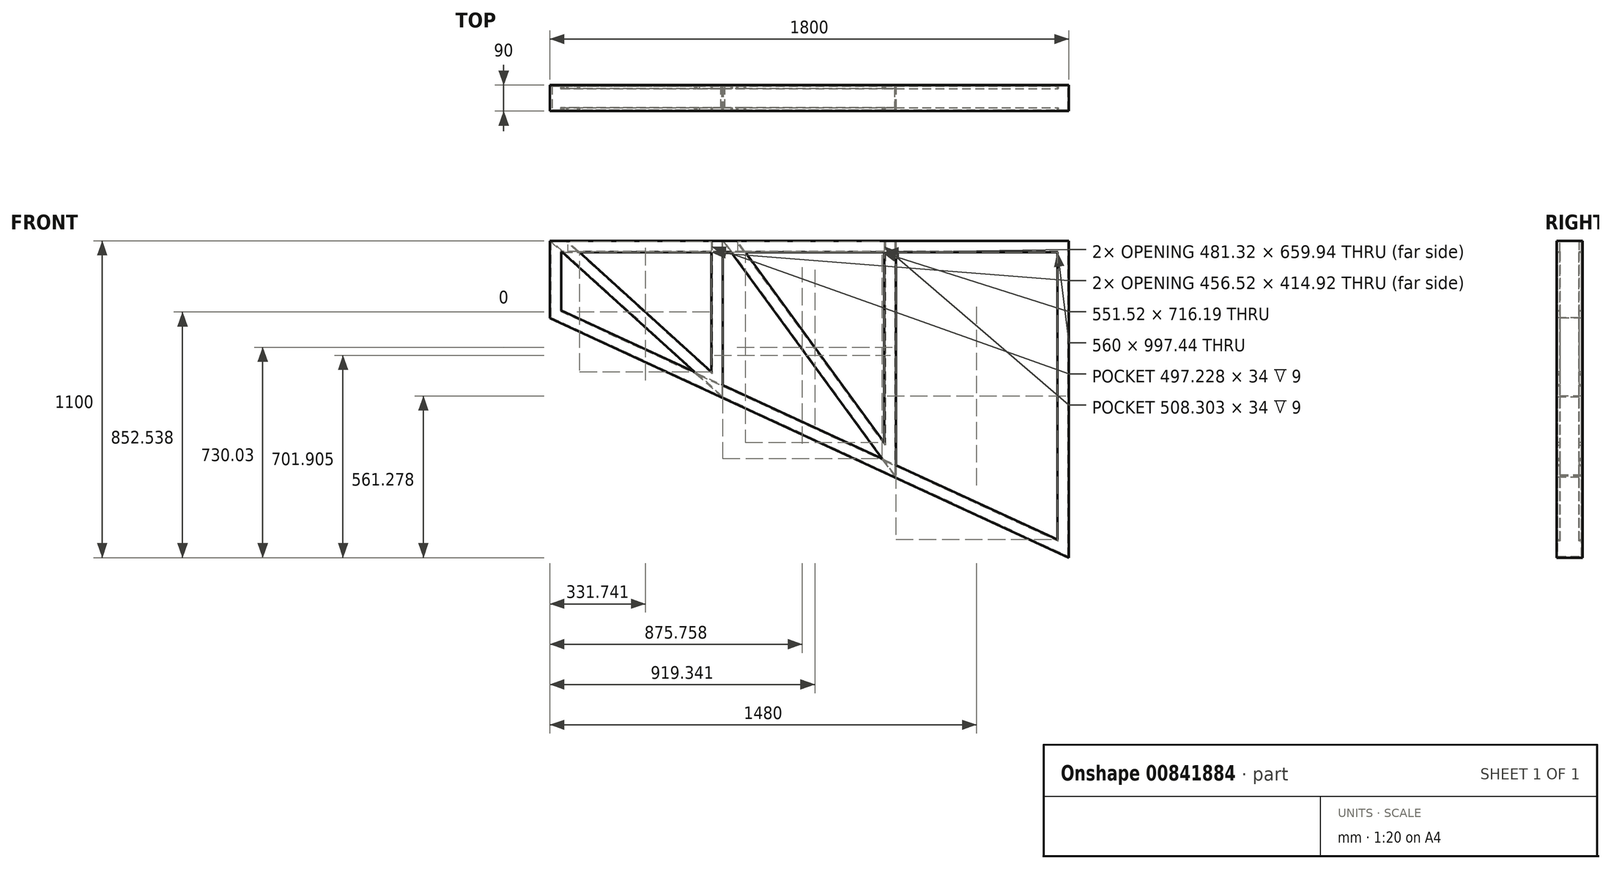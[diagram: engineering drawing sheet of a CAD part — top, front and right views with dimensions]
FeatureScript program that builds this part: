
annotation { "Feature Type Name" : "Feature", "Feature Type Description" : "" }
export const myFeature = defineFeature(function(context is Context, id is Id, definition is map)
    precondition{}
    {
        {
            var Q0;
            Q0=qCreatedBy(makeId("Front.planeOp"),FACE);
            var sketch = newSketch(context, id + "F0", { "sketchPlane" : qUnion([Q0])});
            skLineSegment(sketch, "E0", {"start": v(0, 0) * mm, "end": v(0, 1100) * mm});
            skLineSegment(sketch, "E1", {"start": v(0, 1100) * mm, "end": v(-1800, 1100) * mm});
            skLineSegment(sketch, "E2", {"start": v(-1800, 1100) * mm, "end": v(-1800, 832) * mm});
            skLineSegment(sketch, "E3", {"start": v(-1800, 832) * mm, "end": v(0, 0) * mm});
            skSolve(sketch);
        }
        {
            var Q0;
            Q0=qCreatedBy(makeId("Top.planeOp"),FACE);
            var sketch = newSketch(context, id + "F1", { "sketchPlane" : qUnion([Q0])});
            skLineSegment(sketch, "E4", {"start": v(0, 0) * mm, "end": v(0, -45) * mm});
            skLineSegment(sketch, "E5", {"start": v(0, -45) * mm, "end": v(-40, -45) * mm});
            skLineSegment(sketch, "E6", {"start": v(-40, -45) * mm, "end": v(-40, -33) * mm});
            skLineSegment(sketch, "E7.MirrorCS", {"start": v(-40, 45) * mm, "end": v(-40, 33) * mm});
            skLineSegment(sketch, "E8.MirrorCS", {"start": v(0, 45) * mm, "end": v(-40, 45) * mm});
            skLineSegment(sketch, "E9.MirrorCS", {"start": v(0, 0) * mm, "end": v(0, 45) * mm});
            skLineSegment(sketch, "E10.0", {"start": v(-37, -42) * mm, "end": v(-37, -33) * mm});
            skLineSegment(sketch, "E10.1", {"start": v(-3, -42) * mm, "end": v(-37, -42) * mm});
            skLineSegment(sketch, "E10.2", {"start": v(-37, 42) * mm, "end": v(-37, 33) * mm});
            skLineSegment(sketch, "E10.3", {"start": v(-3, 42) * mm, "end": v(-37, 42) * mm});
            skLineSegment(sketch, "E10.4", {"start": v(-3, 0) * mm, "end": v(-3, 42) * mm});
            skLineSegment(sketch, "E10.5", {"start": v(-3, 0) * mm, "end": v(-3, -42) * mm});
            skLineSegment(sketch, "E11", {"start": v(-40, -33) * mm, "end": v(-37, -33) * mm});
            skLineSegment(sketch, "E12", {"start": v(-40, 33) * mm, "end": v(-37, 33) * mm});
            skSolve(sketch);
        }
        {
            var Q0;
            Q0 = qSketchRegion(id + "F1", true);
            var Q1;
            Q1 = qConstructionFilter(qBodyType(qCreatedBy(id + "F0" ,EDGE), BodyType.WIRE), ConstructionObject.NO);
            sweep(context, id + "F2", {"profiles" : qUnion([Q0]), "path" : qUnion([Q1])});
        }
        {
            var Q0;
            Q0=qCreatedBy(makeId("Front.planeOp"),FACE);
            var sketch = newSketch(context, id + "F3", { "sketchPlane" : qUnion([Q0])});
            skLineSegment(sketch, "E13", {"start": v(-600, 1100) * mm, "end": v(-600, 277.33) * mm});
            skLineSegment(sketch, "E14", {"start": v(-600, 277.33) * mm, "end": v(-1200, 1100) * mm});
            skLineSegment(sketch, "E15", {"start": v(-1200, 1100) * mm, "end": v(-1200, 554.67) * mm});
            skLineSegment(sketch, "E16", {"start": v(-1200, 554.67) * mm, "end": v(-1800, 1100) * mm});
            skSolve(sketch);
        }
        {
            var Q0;
            Q0=makeQuery(id+"F2.opSweep","SWEPT_FACE",FACE,{"disambiguationData":[OSD([sQuery(id+"F0.wireOp",EDGE,"E1"),sQuery(id+"F1.wireOp",EDGE,"E4"),sQuery(id+"F1.wireOp",EDGE,"E9.MirrorCS")])]});
            var sketch = newSketch(context, id + "F4", { "sketchPlane" : qUnion([Q0])});
            skLineSegment(sketch, "E17", {"start": v(-600, 0) * mm, "end": v(-600, 45) * mm});
            skLineSegment(sketch, "E18", {"start": v(-600, 45) * mm, "end": v(-640, 45) * mm});
            skLineSegment(sketch, "E19", {"start": v(-640, 45) * mm, "end": v(-640, 33) * mm});
            skLineSegment(sketch, "E20.MirrorCS", {"start": v(-640, -45) * mm, "end": v(-640, -33) * mm});
            skLineSegment(sketch, "E21.MirrorCS", {"start": v(-600, -45) * mm, "end": v(-640, -45) * mm});
            skLineSegment(sketch, "E22.MirrorCS", {"start": v(-600, 0) * mm, "end": v(-600, -45) * mm});
            skLineSegment(sketch, "E23.0", {"start": v(-637, 42) * mm, "end": v(-637, 33) * mm});
            skLineSegment(sketch, "E23.1", {"start": v(-603, 42) * mm, "end": v(-637, 42) * mm});
            skLineSegment(sketch, "E23.2", {"start": v(-637, -42) * mm, "end": v(-637, -33) * mm});
            skLineSegment(sketch, "E23.3", {"start": v(-603, -42) * mm, "end": v(-637, -42) * mm});
            skLineSegment(sketch, "E23.4", {"start": v(-603, 0) * mm, "end": v(-603, -42) * mm});
            skLineSegment(sketch, "E23.5", {"start": v(-603, 0) * mm, "end": v(-603, 42) * mm});
            skLineSegment(sketch, "E24", {"start": v(-640, 33) * mm, "end": v(-637, 33) * mm});
            skLineSegment(sketch, "E25", {"start": v(-637, -33) * mm, "end": v(-640, -33) * mm});
            skSolve(sketch);
        }
        {
            var Q0;
            Q0 = qSketchRegion(id + "F4", true);
            var Q1;
            Q1 = qConstructionFilter(qBodyType(qCreatedBy(id + "F3" ,EDGE), BodyType.WIRE), ConstructionObject.NO);
            sweep(context, id + "F5", {"operationType" : NewBodyOperationType.ADD, "profiles" : qUnion([Q0]), "path" : qUnion([Q1])});
        }
        {
            var Q0;
            Q0=makeQuery(id+"F2.opSweep","SWEPT_FACE",FACE,{"disambiguationData":[OSD([sQuery(id+"F0.wireOp",EDGE,"E0"),sQuery(id+"F1.wireOp",EDGE,"E4"),sQuery(id+"F1.wireOp",EDGE,"E9.MirrorCS")])]});
            var sketch = newSketch(context, id + "F6", { "sketchPlane" : qUnion([Q0])});
            skLineSegment(sketch, "E26.bottom", {"start": v(45, 1100) * mm, "end": v(-45, 1100) * mm});
            skLineSegment(sketch, "E26.top", {"start": v(45, 1303.9) * mm, "end": v(-45, 1303.9) * mm});
            skLineSegment(sketch, "E26.left", {"start": v(45, 1100) * mm, "end": v(45, 1303.9) * mm});
            skLineSegment(sketch, "E26.right", {"start": v(-45, 1100) * mm, "end": v(-45, 1303.9) * mm});
            skSolve(sketch);
        }
        {
            var Q0;
            Q0 = qSketchRegion(id + "F6", true);
            extrude(context, id + "F7", {"entities" : qUnion([Q0]), "operationType" : NewBodyOperationType.REMOVE, "endBound" : BoundingType.THROUGH_ALL, "oppositeDirection" : true, "depth" : 25 * mm, "offsetDistance" : 25 * mm});
        }
    });
